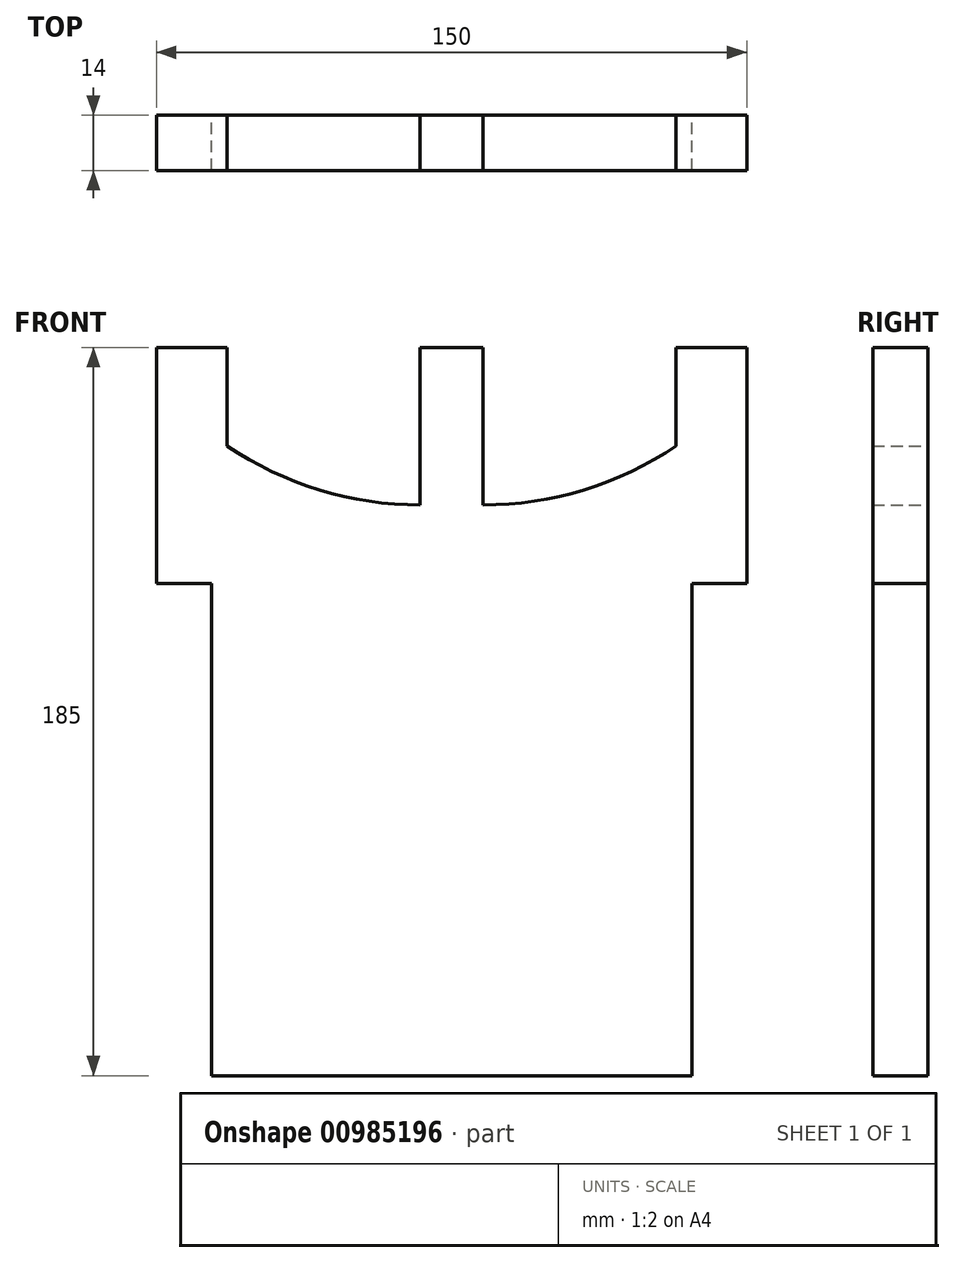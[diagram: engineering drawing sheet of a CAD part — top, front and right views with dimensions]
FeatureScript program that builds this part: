
annotation { "Feature Type Name" : "Feature", "Feature Type Description" : "" }
export const myFeature = defineFeature(function(context is Context, id is Id, definition is map)
    precondition{}
    {
        {
            var Q0;
            Q0=qCreatedBy(makeId("Front.planeOp"),FACE);
            var sketch = newSketch(context, id + "F0", { "sketchPlane" : qUnion([Q0])});
            skLineSegment(sketch, "E0.bottom", {"start": v(-61, 0) * mm, "end": v(0, 0) * mm});
            skLineSegment(sketch, "E0.top", {"start": v(-8, 185) * mm, "end": v(0, 185) * mm});
            skLineSegment(sketch, "E0.left", {"start": v(-75, 125) * mm, "end": v(-75, 185) * mm});
            skLineSegment(sketch, "E0.right", {"start": v(0, 0) * mm, "end": v(0, 185) * mm});
            skLineSegment(sketch, "E1.top", {"start": v(-75, 125) * mm, "end": v(-61, 125) * mm});
            skLineSegment(sketch, "E1.right", {"start": v(-61, 0) * mm, "end": v(-61, 125) * mm});
            skLineSegment(sketch, "E2", {"start": v(-75, 185) * mm, "end": v(-57, 185) * mm});
            skLineSegment(sketch, "E3", {"start": v(0, 185) * mm, "end": v(-8, 185) * mm});
            skLineSegment(sketch, "E4", {"start": v(-8, 185) * mm, "end": v(-8, 145) * mm});
            skLineSegment(sketch, "E5", {"start": v(-57, 185) * mm, "end": v(-57, 160) * mm});
            skArc(sketch, "E6", {"start": v(-57, 160) * mm, "mid": v(-33.62, 148.83) * mm, "end": v(-8, 145) * mm});
            skLineSegment(sketch, "E7.MirrorCS", {"start": v(0, 185) * mm, "end": v(8, 185) * mm});
            skLineSegment(sketch, "E8.MirrorCS", {"start": v(8, 185) * mm, "end": v(0, 185) * mm});
            skLineSegment(sketch, "E9.MirrorCS", {"start": v(61, 0) * mm, "end": v(0, 0) * mm});
            skLineSegment(sketch, "E10.MirrorCS", {"start": v(57, 185) * mm, "end": v(57, 160) * mm});
            skLineSegment(sketch, "E11.MirrorCS", {"start": v(61, 0) * mm, "end": v(61, 125) * mm});
            skArc(sketch, "E12.MirrorCS", {"start": v(57, 160) * mm, "mid": v(33.62, 148.83) * mm, "end": v(8, 145) * mm});
            skLineSegment(sketch, "E13.MirrorCS", {"start": v(75, 125) * mm, "end": v(75, 185) * mm});
            skLineSegment(sketch, "E14.MirrorCS", {"start": v(8, 185) * mm, "end": v(8, 145) * mm});
            skLineSegment(sketch, "E15.MirrorCS", {"start": v(75, 185) * mm, "end": v(57, 185) * mm});
            skLineSegment(sketch, "E16.MirrorCS", {"start": v(75, 125) * mm, "end": v(61, 125) * mm});
            skSolve(sketch);
        }
        {
            var Q0;
            Q0=makeQuery(id+"F0.imprint","IMPRINT",FACE,{"disambiguationData":[TD([[makeQuery(id+"F0.imprint","IMPRINT",EDGE,{"derivedFrom":sQuery(id+"F0.wireOp",EDGE,"E0.right")}),-1.0]])]});
            var Q1;
            Q1=makeQuery(id+"F0.imprint","IMPRINT",FACE,{"disambiguationData":[TD([[makeQuery(id+"F0.imprint","IMPRINT",EDGE,{"derivedFrom":sQuery(id+"F0.wireOp",EDGE,"E0.bottom")}),1.0]])]});
            extrude(context, id + "F1", {"entities" : qUnion([Q0, Q1]), "depth" : 14 * mm, "offsetDistance" : 25 * mm});
        }
    });
